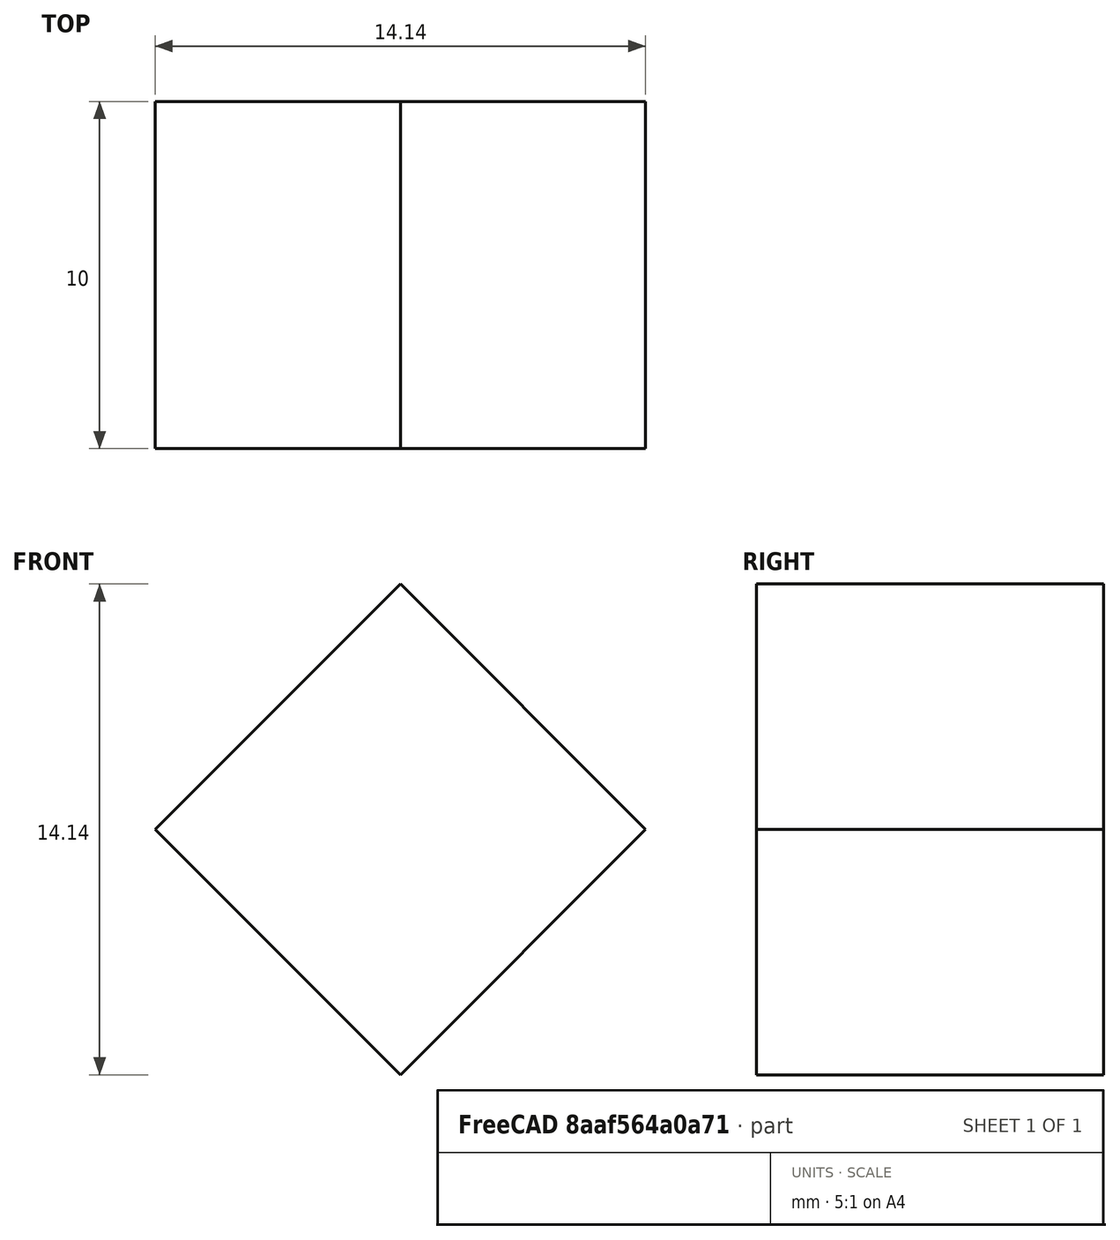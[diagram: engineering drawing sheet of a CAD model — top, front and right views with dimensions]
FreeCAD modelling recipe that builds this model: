
FCSTD DOCUMENT  (FreeCAD 0.21R33694 (Git))
Label: VM_Uniaxial_Tension_Example
License: All rights reserved
LicenseURL: http://en.wikipedia.org/wiki/All_rights_reserved
objects: Fem::ConstraintPressure×3, Fem::FemMeshObjectPython×2, Fem::ConstraintDisplacement×2, Part::Box×1, Fem::FemSolverObjectPython×1, App::MaterialObjectPython×1, Fem::ConstraintFixed×1, Fem::FemPostPipeline×1, Fem::FemResultObjectPython×1, Fem::FemAnalysis×1
note: 1 computed .brp shape members not serialized (recipe doc carries the construction recipe); baked Part::Feature solids carry a one-line shape summary decoded from their .brp

FEATURE [Part::Box] Box  label="Cube"
  AttacherType = Attacher::AttachEngine3D
  Height = 10
  Length = 10
  Placement = pos=(0,0,0) rot=(0,1,0;0.785398rad)
  Width = 10
FEATURE [Fem::FemSolverObjectPython] SolverCcxTools  # FEM object (typed FeaturePython)
  AnalysisType = 0
  BeamShellResultOutput3D = false
  BucklingFactors = 1
  EigenmodeHighLimit = 1000000
  EigenmodeLowLimit = 0
  EigenmodesCount = 10
  GeometricalNonlinearity = 0
  IterationsControlParameterCutb = 0.25,0.5,0.75,0.85,,,1.5,
  IterationsControlParameterIter = 4,8,9,200,10,400,,200,,
  IterationsControlParameterTimeUse = false
  IterationsThermoMechMaximum = 2000
  IterationsUserDefinedIncrementations = false
  IterationsUserDefinedTimeStepLength = false
  MaterialNonlinearity = 0
  MatrixSolverType = 0
  SplitInputWriter = false
  ThermoMechSteadyState = true
  TimeEnd = 1
  TimeInitialStep = 0.01
FEATURE [Fem::FemMeshObjectPython] FEMMeshGmsh  # FEM object (typed FeaturePython)
  Algorithm2D = 0
  Algorithm3D = 0
  CharacteristicLengthMax = 10
  CharacteristicLengthMin = 10
  CoherenceMesh = true
  ElementDimension = 0
  ElementOrder = 1
  GeometryTolerance = 1e-06
  GroupsOfNodes = false
  HighOrderOptimize = 0
  MeshSizeFromCurvature = 12
  OptimizeNetgen = false
  OptimizeStd = true
  Part = -> Box
  RecombinationAlgorithm = 0
  Recombine3DAll = false
  RecombineAll = false
  SecondOrderLinear = false
FEATURE [Fem::ConstraintPressure] ConstraintPressure
  NormalDirection = (0.707107,0,-0.707107)
  Normals = (18) [(0.707107,0,-0.707107),(0.707107,0,-0.707107),(0.707107,0,-0.707107),(0.707107,0,-0.707107),(0.707107,0,-0.707107),(0.707107,0,-0.707107),+12 more]
  Points = (18) [(7.07107,10,-7.07107),(10.6066,10,-3.53553),(14.1421,10,-9.76996e-15),(7.07107,5,-7.07107),(10.6066,5,-3.53553),(14.1421,5,-9.76996e-15),+12 more]
  Pressure = 0
  References = -> [Box]
  Reversed = true
FEATURE [App::MaterialObjectPython] MaterialSolid  # material (typed FeaturePython)
  Category = 0
  Material = AuthorAndLicense=(c) 2013 Yorik van Havre (CC-BY 3.0),CardName=Concrete-Generic,CompressiveStrength=25 MPa,Density=2400 kg/m^3,+7 more (map truncated)
  References = -> [Box]
FEATURE [Fem::ConstraintPressure] ConstraintPressure001
  NormalDirection = (0,-1,0)
  Normals = (18) [(0,-1,0),(0,-1,0),(0,-1,0),(0,-1,0),(0,-1,0),(0,-1,0),(0,-1,0),(0,-1,0),(0,-1,0),(0,1,0),(0,1,0),(0,1,0),(0,1,0),(0,1,0),(0,1,0),(0,1,0),(0,1,0),+1 more]
  Points = (18) [(0,0,0),(3.53553,0,3.53553),(7.07107,0,7.07107),(3.53553,0,-3.53553),(7.07107,0,-4.88498e-15),(10.6066,0,3.53553),(7.07107,0,-7.07107),+11 more]
  Pressure = 0
  References = -> [Box]
FEATURE [Fem::ConstraintPressure] ConstraintPressure002
  NormalDirection = (0.707107,0,0.707107)
  Normals = (18) [(0.707107,0,0.707107),(0.707107,0,0.707107),(0.707107,0,0.707107),(0.707107,0,0.707107),(0.707107,0,0.707107),(0.707107,0,0.707107),+12 more]
  Points = (18) [(7.07107,0,7.07107),(10.6066,0,3.53553),(14.1421,0,-9.76996e-15),(7.07107,5,7.07107),(10.6066,5,3.53553),(14.1421,5,-9.76996e-15),+12 more]
  Pressure = 100
  References = -> [Box]
  Reversed = true
FEATURE [Fem::ConstraintFixed] ConstraintFixed
  NormalDirection = (0,0,1)
  Normals = (1) [(0,0,1)]
  Points = (1) [(0,0,0)]
  References = -> [Box]
  Scale = 2
FEATURE [Fem::ConstraintDisplacement] ConstraintDisplacement
  NormalDirection = (0,0,1)
  Normals = (2) [(0,0,1),(0,0,1)]
  Points = (2) [(0,10,0),(7.07107,0,-7.07107)]
  References = -> [Box]
  Scale = 2
  hasXFormula = false
  hasYFormula = false
  hasZFormula = false
  rotxFix = false
  rotxFree = true
  rotyFix = false
  rotyFree = true
  rotzFix = false
  rotzFree = true
  useFlowSurfaceForce = false
  xDisplacement = 0
  xFix = false
  xFree = true
  xRotation = 0
  yDisplacement = 0
  yFix = false
  yFree = true
  yRotation = 0
  zDisplacement = 0
  zFix = false
  zFree = false
  zRotation = 0
FEATURE [Fem::ConstraintDisplacement] ConstraintDisplacement001
  NormalDirection = (0,0,1)
  Normals = (1) [(0,0,1)]
  Points = (1) [(0,10,0)]
  References = -> [Box]
  Scale = 2
  hasXFormula = false
  hasYFormula = false
  hasZFormula = false
  rotxFix = false
  rotxFree = true
  rotyFix = false
  rotyFree = true
  rotzFix = false
  rotzFree = true
  useFlowSurfaceForce = false
  xDisplacement = 0
  xFix = false
  xFree = false
  xRotation = 0
  yDisplacement = 0
  yFix = false
  yFree = true
  yRotation = 0
  zDisplacement = 0
  zFix = false
  zFree = true
  zRotation = 0
FEATURE [Fem::FemPostPipeline] Pipeline_CCX_Results
  Mode = 2
FEATURE [Fem::FemMeshObjectPython] Result_Mesh_Volume  # FEM object (typed FeaturePython)
FEATURE [Fem::FemResultObjectPython] ResultMechanical  # FEM object (typed FeaturePython)
  CriticalStrainRatio = [0,0,0,0,0,0,0,0,0,0,0,0,0,0,0,0,0,0,0,0,0,0,0,0,0,0,0,0,0,0,0,0,0,0,0,0,0,0,0,0,0,0,0,0,0,0,0,0,0,0,0,0,0,0,0,0,0,0,0,0,0,0,0]
  DisplacementLengths = [0.0130861,0,0.0130861,4.79002e-18,0.0130862,2.27861e-07,0.0130862,2.27861e-07,0.00654304,0.0130861,0.00654304,5.00609e-17,0.0065432,0.0130862,0.0065432,2.27861e-07,1.13931e-07,0.0130862,1.13931e-07,0.0130862,0.00654304,0.00981456,+41 more]
  DisplacementVectors = (63) [(0.00925315,-2.50375e-17,0.00925337),(0,0,0),(0.00925315,-1.56863e-17,0.00925337),(0,-4.79002e-18,0),(0.00925337,6.16019e-17,0.00925337),+58 more]
  Eigenmode = 0
  EigenmodeFrequency = 0
  Mesh = -> Result_Mesh_Volume
  NodeNumbers = [1,2,3,4,5,6,7,8,9,10,11,12,13,14,15,16,17,18,19,20,21,22,23,24,25,26,27,28,29,30,31,32,33,34,35,36,37,38,39,40,41,42,43,44,45,46,47,48,49,50,51,52,53,54,55,56,57,58,59,60,61,62,63]
  NodeStressXX = [0.870146,0.870146,0.870146,0.870146,0.870146,0.870146,0.870146,0.870146,0.870146,0.870146,0.870146,0.870146,0.870146,0.870146,0.870146,0.870146,0.870146,0.870146,0.870146,0.870146,0.870146,0.870146,0.870146,0.870146,0.870146,0.870146,+37 more]
  NodeStressXY = [-3.14123e-15,1.19503e-15,6.04345e-15,-5.15571e-15,-5.36057e-15,3.8241e-15,-1.39989e-15,4.50698e-15,-9.73098e-16,1.45111e-15,4.43869e-16,-1.98034e-15,-7.68235e-16,-3.38023e-15,1.55354e-15,4.16554e-15,2.50957e-15,-4.2509e-15,-3.24366e-16,+44 more]
  NodeStressXZ = [0.869854,0.869854,0.869854,0.869854,0.869854,0.869854,0.869854,0.869854,0.869854,0.869854,0.869854,0.869854,0.869854,0.869854,0.869854,0.869854,0.869854,0.869854,0.869854,0.869854,0.869854,0.869854,0.869854,0.869854,0.869854,0.869854,+37 more]
  NodeStressYY = [-8.31603e-15,-1.55769e-15,1.13127e-14,-6.15955e-15,-1.95469e-16,-4.53144e-15,-2.37246e-14,-1.80978e-15,-4.93686e-15,1.49833e-15,2.57657e-15,-3.85862e-15,-2.36345e-15,-1.19601e-14,-1.27672e-14,-3.17061e-15,-3.04457e-15,-4.25575e-15,+45 more]
  NodeStressYZ = [3.14123e-15,-1.19503e-15,-6.04345e-15,5.15571e-15,5.36057e-15,-3.8241e-15,1.39989e-15,-4.50698e-15,9.73098e-16,-1.45111e-15,-4.43869e-16,1.98034e-15,7.68235e-16,3.38023e-15,-1.55354e-15,-4.16554e-15,-2.50957e-15,4.2509e-15,3.24366e-16,+44 more]
  NodeStressZZ = [0.870146,0.870146,0.870146,0.870146,0.870146,0.870146,0.870146,0.870146,0.870146,0.870146,0.870146,0.870146,0.870146,0.870146,0.870146,0.870146,0.870146,0.870146,0.870146,0.870146,0.870146,0.870146,0.870146,0.870146,0.870146,0.870146,+37 more]
  Peeq = [0.00165033,0.00165033,0.00165033,0.00165033,0.00165033,0.00165033,0.00165033,0.00165033,0.00165033,0.00165033,0.00165033,0.00165033,0.00165033,0.00165033,0.00165033,0.00165033,0.00165033,0.00165033,0.00165033,0.00165033,0.00165033,+42 more]
  ResultType = Fem::ResultMechanical
  Stats = [0,0.00925337,-4.93811e-17,6.47294e-17,0,0.00925337,0,0.0130862,0,0,0,0,0,0,0,0,0,0,0.00165033,0.00165033,0,0,0,0,0,0]
  Temperature = [0,0,0,0,0,0,0,0,0,0,0,0,0,0,0,0,0,0,0,0,0,0,0,0,0,0,0,0,0,0,0,0,0,0,0,0,0,0,0,0,0,0,0,0,0,0,0,0,0,0,0,0,0,0,0,0,0,0,0,0,0,0,0]
  Time = 0
  vonMises = [0,0,0,0,0,0,0,0,0,0,0,0,0,0,0,0,0,0,0,0,0,0,0,0,0,0,0,0,0,0,0,0,0,0,0,0,0,0,0,0,0,0,0,0,0,0,0,0,0,0,0,0,0,0,0,0,0,0,0,0,0,0,0]
FEATURE [Fem::FemAnalysis] Analysis
  Group = -> [SolverCcxTools,FEMMeshGmsh,ConstraintPressure,MaterialSolid,ConstraintPressure001,ConstraintPressure002,ConstraintFixed,ConstraintDisplacement,ConstraintDisplacement001,Pipeline_CCX_Results,ResultMechanical]
